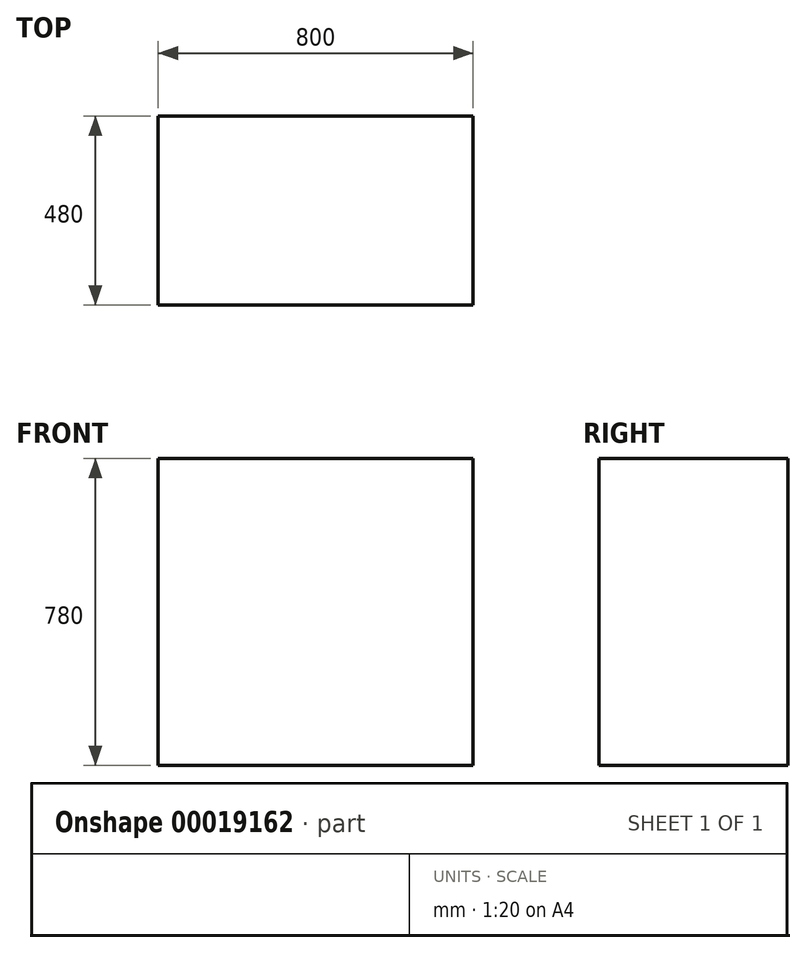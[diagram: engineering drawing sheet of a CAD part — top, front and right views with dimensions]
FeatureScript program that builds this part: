
annotation { "Feature Type Name" : "Feature", "Feature Type Description" : "" }
export const myFeature = defineFeature(function(context is Context, id is Id, definition is map)
    precondition{}
    {
        {
            var Q0;
            Q0=qCreatedBy(makeId("Top.planeOp"),FACE);
            var sketch = newSketch(context, id + "F0", { "sketchPlane" : qUnion([Q0])});
            skLineSegment(sketch, "E0.bottom", {"start": v(0, 0) * mm, "end": v(800, 0) * mm});
            skLineSegment(sketch, "E0.top", {"start": v(0, 480) * mm, "end": v(800, 480) * mm});
            skLineSegment(sketch, "E0.left", {"start": v(0, 0) * mm, "end": v(0, 480) * mm});
            skLineSegment(sketch, "E0.right", {"start": v(800, 0) * mm, "end": v(800, 480) * mm});
            skSolve(sketch);
        }
        {
            var Q0;
            Q0=makeQuery(id+"F0.imprint","IMPRINT",FACE,{"disambiguationData":[TD([[makeQuery(id+"F0.imprint","IMPRINT",EDGE,{"derivedFrom":sQuery(id+"F0.wireOp",EDGE,"E0.bottom")}),1.0]])]});
            extrude(context, id + "F1", {"entities" : qUnion([Q0]), "depth" : 780 * mm});
        }
    });
